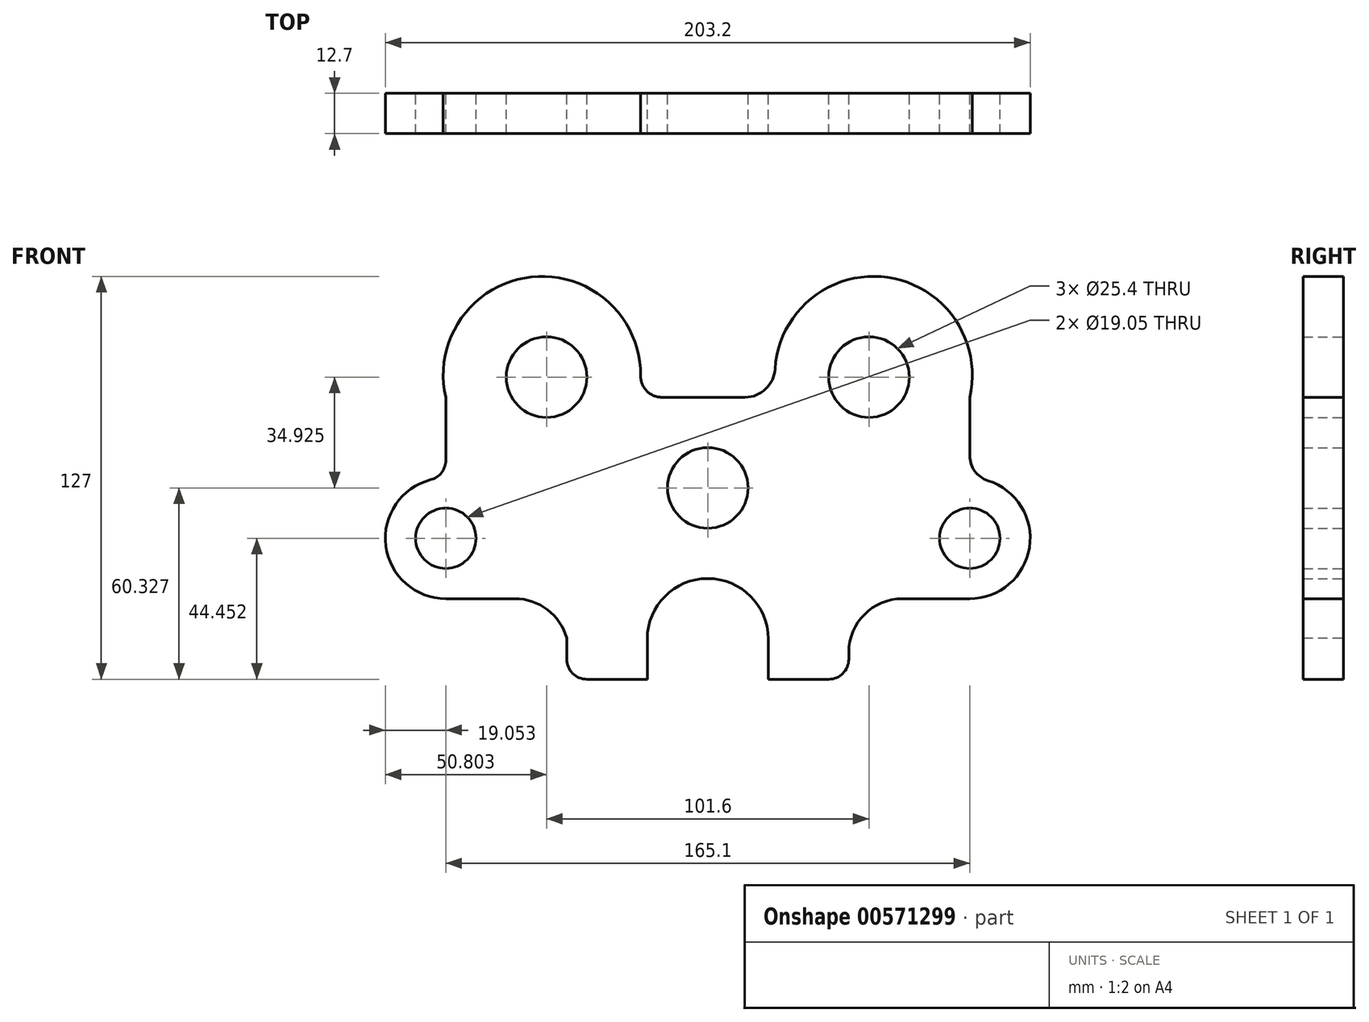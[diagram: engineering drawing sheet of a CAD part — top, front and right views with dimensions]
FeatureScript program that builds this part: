
annotation { "Feature Type Name" : "Feature", "Feature Type Description" : "" }
export const myFeature = defineFeature(function(context is Context, id is Id, definition is map)
    precondition{}
    {
        {
            var Q0;
            Q0=qCreatedBy(makeId("Front.planeOp"),FACE);
            var sketch = newSketch(context, id + "F0", { "sketchPlane" : qUnion([Q0])});
            skLineSegment(sketch, "E0", {"start": v(-0.06, 105.29) * mm, "end": v(-0.06, -145.8) * mm, "construction": true});
            skLineSegment(sketch, "E1", {"start": v(-0.06, 43.5) * mm, "end": v(11.7, 43.5) * mm});
            skArc(sketch, "E2", {"start": v(82.5, 43.5) * mm, "mid": v(56.65, 81.27) * mm, "end": v(21.14, 52.38) * mm});
            skLineSegment(sketch, "E3", {"start": v(82.5, 43.5) * mm, "end": v(82.5, 25.05) * mm});
            skArc(sketch, "E4", {"start": v(82.5, -20) * mm, "mid": v(101.32, -3.87) * mm, "end": v(88.24, 17.2) * mm});
            skLineSegment(sketch, "E5", {"start": v(38.04, -45.4) * mm, "end": v(19, -45.4) * mm});
            skLineSegment(sketch, "E6.MirrorCS", {"start": v(-0.06, 43.5) * mm, "end": v(-14.53, 43.5) * mm});
            skArc(sketch, "E7.MirrorCS", {"start": v(-82.6, 43.5) * mm, "mid": v(-55.69, 81.4) * mm, "end": v(-21.2, 50.22) * mm});
            skLineSegment(sketch, "E8.MirrorCS", {"start": v(-82.6, 43.5) * mm, "end": v(-82.6, 23.64) * mm});
            skArc(sketch, "E9.MirrorCS", {"start": v(-82.6, -20) * mm, "mid": v(-101.5, -3.36) * mm, "end": v(-87.37, 17.49) * mm});
            skLineSegment(sketch, "E10.MirrorCS", {"start": v(-38.16, -45.4) * mm, "end": v(-19.1, -45.4) * mm});
            skCircle(sketch, "E11", {"center": v(-0.06, 14.92) * mm, "radius": 12.7 * mm});
            skPoint(sketch, "E12.visualSharp", {"position": v(82.5, 18.1) * mm});
            skArc(sketch, "E12.filletArc", {"start": v(82.5, 25.05) * mm, "mid": v(84.08, 20.19) * mm, "end": v(88.24, 17.2) * mm});
            skPoint(sketch, "E13.visualSharp", {"position": v(21.88, 43.5) * mm});
            skArc(sketch, "E13.filletArc", {"start": v(11.7, 43.5) * mm, "mid": v(18.18, 46.06) * mm, "end": v(21.14, 52.38) * mm});
            skPoint(sketch, "E14.visualSharp", {"position": v(-22, 43.5) * mm});
            skArc(sketch, "E14.filletArc", {"start": v(-21.2, 50.22) * mm, "mid": v(-19.27, 45.47) * mm, "end": v(-14.53, 43.5) * mm});
            skPoint(sketch, "E15.visualSharp", {"position": v(-82.6, 18.1) * mm});
            skArc(sketch, "E15.filletArc", {"start": v(-87.37, 17.49) * mm, "mid": v(-83.94, 19.75) * mm, "end": v(-82.6, 23.64) * mm});
            skCircle(sketch, "E16", {"center": v(-50.86, 49.84) * mm, "radius": 12.7 * mm});
            skCircle(sketch, "E17", {"center": v(50.74, 49.84) * mm, "radius": 12.7 * mm});
            skLineSegment(sketch, "E18", {"start": v(-19.1, -45.4) * mm, "end": v(-19.1, -32.7) * mm});
            skLineSegment(sketch, "E19", {"start": v(-0.06, -13.66) * mm, "end": v(-0.06, -13.66) * mm});
            skLineSegment(sketch, "E20", {"start": v(19, -32.7) * mm, "end": v(19, -45.4) * mm});
            skPoint(sketch, "E21.visualSharp", {"position": v(-19.1, -13.66) * mm});
            skArc(sketch, "E21.filletArc", {"start": v(-0.06, -13.66) * mm, "mid": v(-13.53, -19.24) * mm, "end": v(-19.1, -32.7) * mm});
            skPoint(sketch, "E22.visualSharp", {"position": v(19, -13.66) * mm});
            skArc(sketch, "E22.filletArc", {"start": v(19, -32.7) * mm, "mid": v(13.41, -19.24) * mm, "end": v(-0.06, -13.66) * mm});
            skLineSegment(sketch, "E23", {"start": v(-82.6, -20) * mm, "end": v(-60.82, -20) * mm});
            skPoint(sketch, "E24.visualSharp", {"position": v(-37.22, -20) * mm});
            skArc(sketch, "E24.filletArc", {"start": v(-44.5, -32.4) * mm, "mid": v(-50.58, -23.46) * mm, "end": v(-60.82, -20) * mm});
            skLineSegment(sketch, "E25", {"start": v(82.5, -20) * mm, "end": v(61.33, -20) * mm});
            skLineSegment(sketch, "E26", {"start": v(44.4, -36.94) * mm, "end": v(44.4, -39.06) * mm});
            skPoint(sketch, "E27.visualSharp", {"position": v(44.4, -20) * mm});
            skArc(sketch, "E27.filletArc", {"start": v(61.33, -20) * mm, "mid": v(49.35, -24.97) * mm, "end": v(44.4, -36.94) * mm});
            skLineSegment(sketch, "E28", {"start": v(-44.5, -32.4) * mm, "end": v(-44.5, -39.06) * mm});
            skPoint(sketch, "E29.visualSharp", {"position": v(44.4, -45.4) * mm});
            skArc(sketch, "E29.filletArc", {"start": v(38.04, -45.4) * mm, "mid": v(42.53, -43.55) * mm, "end": v(44.4, -39.06) * mm});
            skPoint(sketch, "E30.visualSharp", {"position": v(-44.5, -45.4) * mm});
            skArc(sketch, "E30.filletArc", {"start": v(-44.5, -39.06) * mm, "mid": v(-42.65, -43.55) * mm, "end": v(-38.16, -45.4) * mm});
            skCircle(sketch, "E31", {"center": v(-82.6, -0.96) * mm, "radius": 9.53 * mm});
            skCircle(sketch, "E32", {"center": v(82.5, -0.96) * mm, "radius": 9.53 * mm});
            skSolve(sketch);
        }
        {
            var Q0;
            Q0=makeQuery(id+"F0.imprint","IMPRINT",FACE,{"disambiguationData":[TD([[makeQuery(id+"F0.imprint","IMPRINT",EDGE,{"derivedFrom":sQuery(id+"F0.wireOp",EDGE,"E1")}),-1.0]])]});
            extrude(context, id + "F1", {"entities" : qUnion([Q0]), "endBound" : BoundingType.SYMMETRIC, "depth" : 12.7 * mm, "offsetDistance" : 25.4 * mm});
        }
    });
